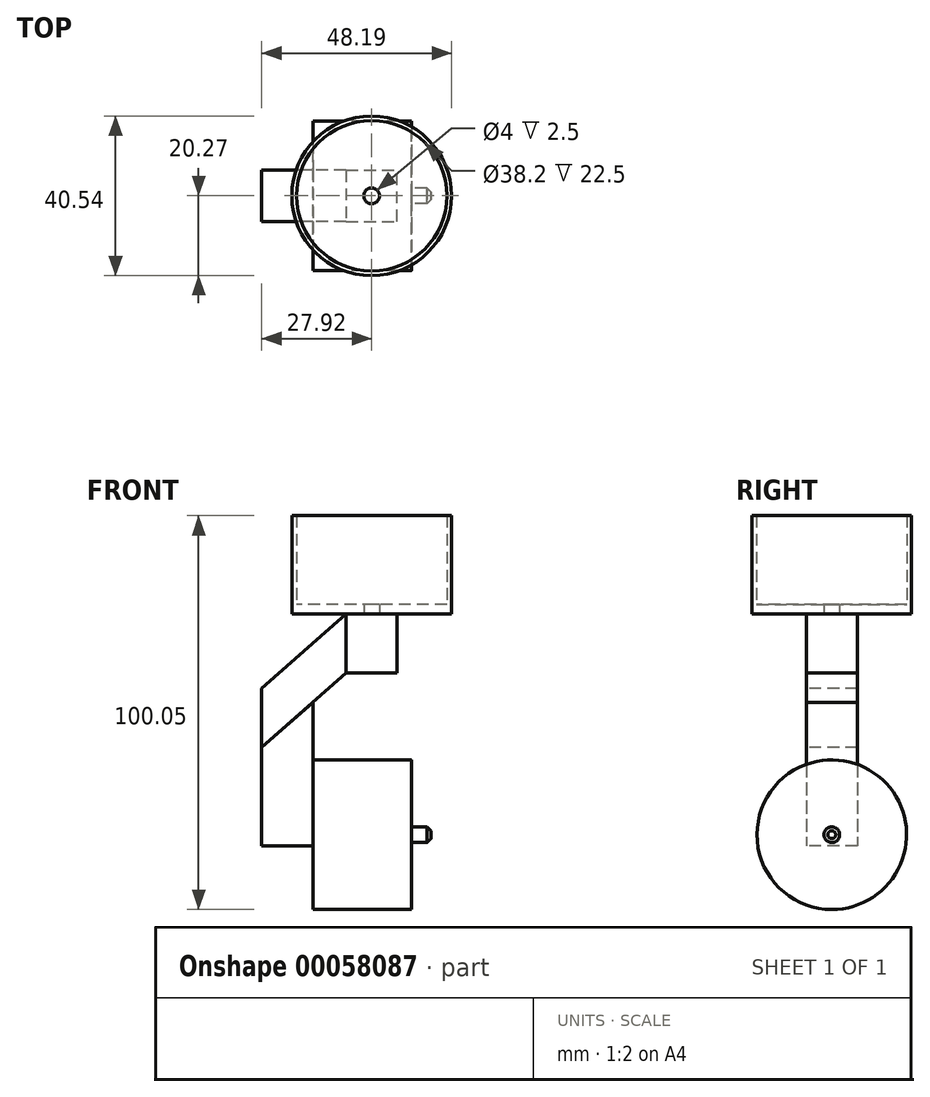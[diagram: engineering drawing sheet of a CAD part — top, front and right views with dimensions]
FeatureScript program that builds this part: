
annotation { "Feature Type Name" : "Feature", "Feature Type Description" : "" }
export const myFeature = defineFeature(function(context is Context, id is Id, definition is map)
    precondition{}
    {
        {
            var Q0;
            Q0=qCreatedBy(makeId("Top.planeOp"),FACE);
            var sketch = newSketch(context, id + "F0", { "sketchPlane" : qUnion([Q0])});
            skCircle(sketch, "E0", {"center": v(0, 0) * mm, "radius": 19.1 * mm});
            skCircle(sketch, "E1", {"center": v(0, 0) * mm, "radius": 20.27 * mm});
            skCircle(sketch, "E2", {"center": v(0, 0) * mm, "radius": 2 * mm});
            skSolve(sketch);
        }
        {
            var Q0;
            Q0=makeQuery(id+"F0.imprint","IMPRINT",FACE,{"disambiguationData":[TD([[makeQuery(id+"F0.imprint","IMPRINT",EDGE,{"derivedFrom":sQuery(id+"F0.wireOp",EDGE,"E0")}),1.0]])]});
            extrude(context, id + "F1", {"entities" : qUnion([Q0]), "depth" : 2.5 * mm});
        }
        {
            var Q0;
            Q0 = qSketchRegion(id + "F0", true);
            extrude(context, id + "F2", {"entities" : qUnion([Q0]), "operationType" : NewBodyOperationType.ADD, "depth" : 25 * mm});
        }
        {
            var Q0;
            {var subQ0=sQuery(id+"F0.wireOp",EDGE,"E0");Q0=makeQuery(id+"F2.boolean.opBoolean","MERGE",FACE,{"derivedFrom":[makeQuery(id+"F1.opExtrude","CAP_FACE",FACE,{"disambiguationData":[OSD([subQ0,sQuery(id+"F0.wireOp",EDGE,"E2")])],"isStart":true}),makeQuery(id+"F2.opExtrude","CAP_FACE",FACE,{"disambiguationData":[OSD([subQ0,sQuery(id+"F0.wireOp",EDGE,"E1")])],"isStart":true})]});}
            var sketch = newSketch(context, id + "F3", { "sketchPlane" : qUnion([Q0])});
            skLineSegment(sketch, "E3.rect.bottom", {"start": v(-6.5, 6.5) * mm, "end": v(6.5, 6.5) * mm});
            skLineSegment(sketch, "E3.rect.top", {"start": v(-6.5, -6.5) * mm, "end": v(6.5, -6.5) * mm});
            skLineSegment(sketch, "E3.rect.left", {"start": v(-6.5, 6.5) * mm, "end": v(-6.5, -6.5) * mm});
            skLineSegment(sketch, "E3.rect.right", {"start": v(6.5, 6.5) * mm, "end": v(6.5, -6.5) * mm});
            skPoint(sketch, "E3.rect.middle", {"position": v(0, 0) * mm});
            skSolve(sketch);
        }
        {
            var Q0;
            Q0=makeQuery(id+"F3.imprint","IMPRINT",FACE,{"disambiguationData":[TD([[makeQuery(id+"F3.imprint","IMPRINT",EDGE,{"derivedFrom":makeQuery(id+"F1.opExtrude","CAP_EDGE",EDGE,{"disambiguationData":[OSD([sQuery(id+"F0.wireOp",EDGE,"E2")])],"isStart":true})}),-1.0]])]});
            var Q1;
            Q1=makeQuery(id+"F3.imprint","IMPRINT",FACE,{"disambiguationData":[TD([[makeQuery(id+"F3.imprint","IMPRINT",EDGE,{"derivedFrom":sQuery(id+"F3.wireOp",EDGE,"E3.rect.bottom")}),-1.0]])]});
            extrude(context, id + "F4", {"entities" : qUnion([Q0, Q1]), "operationType" : NewBodyOperationType.ADD, "depth" : 15 * mm});
        }
        {
            var Q0;
            Q0=makeQuery(id+"F4.opExtrude","SWEPT_FACE",FACE,{"disambiguationData":[OSD([sQuery(id+"F3.wireOp",EDGE,"E3.rect.bottom")])]});
            var sketch = newSketch(context, id + "F5", { "sketchPlane" : qUnion([Q0])});
            skLineSegment(sketch, "E4", {"start": v(-6.5, -15) * mm, "end": v(-27.92, -33.91) * mm});
            skLineSegment(sketch, "E5", {"start": v(-27.92, -33.91) * mm, "end": v(-27.92, -18.91) * mm});
            skLineSegment(sketch, "E6", {"start": v(-6.5, 0) * mm, "end": v(-27.92, -18.91) * mm});
            skSolve(sketch);
        }
        {
            var Q0;
            Q0=makeQuery(id+"F5.imprint","IMPRINT",FACE,{"disambiguationData":[TD([[makeQuery(id+"F5.imprint","IMPRINT",EDGE,{"derivedFrom":sQuery(id+"F5.wireOp",EDGE,"E4")}),-1.0]])]});
            extrude(context, id + "F6", {"entities" : qUnion([Q0]), "oppositeDirection" : true, "depth" : 13 * mm});
        }
        {
            var Q0;
            Q0=makeQuery(id+"F6.opExtrude","CAP_FACE",FACE,{"disambiguationData":[OSD([sQuery(id+"F3.wireOp",EDGE,"E3.rect.bottom"),sQuery(id+"F3.wireOp",EDGE,"E3.rect.left"),sQuery(id+"F5.wireOp",EDGE,"E4"),sQuery(id+"F5.wireOp",EDGE,"E5"),sQuery(id+"F5.wireOp",EDGE,"E6")])],"isStart":true});
            var sketch = newSketch(context, id + "F7", { "sketchPlane" : qUnion([Q0])});
            skLineSegment(sketch, "E7", {"start": v(-27.92, -33.91) * mm, "end": v(-27.92, -58.9) * mm});
            skLineSegment(sketch, "E8", {"start": v(-14.92, -22.43) * mm, "end": v(-14.92, -58.93) * mm});
            skLineSegment(sketch, "E9", {"start": v(-14.92, -58.93) * mm, "end": v(-27.92, -58.9) * mm});
            skSolve(sketch);
        }
        {
            var Q0;
            Q0 = qSketchRegion(id + "F7", true);
            var Q1;
            {var subQ0=sQuery(id+"F7.wireOp",EDGE,"E7");Q1=makeQuery(id+"F7.imprint","IMPRINT",FACE,{"disambiguationData":[TD([[makeQuery(id+"F7.imprint","IMPRINT",EDGE,{"derivedFrom":subQ0}),1.0]])]});}
            extrude(context, id + "F8", {"entities" : qUnion([Q0, Q1]), "oppositeDirection" : true, "depth" : 13 * mm});
        }
        {
            var Q0;
            Q0=makeQuery(id+"F8.opExtrude","SWEPT_FACE",FACE,{"disambiguationData":[OSD([sQuery(id+"F7.wireOp",EDGE,"E8")])]});
            var sketch = newSketch(context, id + "F9", { "sketchPlane" : qUnion([Q0])});
            skCircle(sketch, "E10", {"center": v(0, -56.05) * mm, "radius": 19 * mm});
            skSolve(sketch);
        }
        {
            var Q0;
            {var subQ1=sQuery(id+"F7.wireOp",EDGE,"E8");var subQ6=makeQuery(id+"F8.opExtrude","SWEPT_EDGE",EDGE,{"disambiguationData":[OSD([subQ1,sQuery(id+"F7.wireOp",EDGE,"E9")])]});Q0=makeQuery(id+"F9.imprint","IMPRINT",FACE,{"disambiguationData":[TD([[makeQuery(id+"F9.imprint","IMPRINT",EDGE,{"derivedFrom":subQ6}),-1.0]])]});}
            var Q1;
            {var subQ1=sQuery(id+"F7.wireOp",EDGE,"E8");var subQ6=makeQuery(id+"F8.opExtrude","SWEPT_EDGE",EDGE,{"disambiguationData":[OSD([subQ1,sQuery(id+"F7.wireOp",EDGE,"E9")])]});Q1=makeQuery(id+"F9.imprint","IMPRINT",FACE,{"disambiguationData":[TD([[makeQuery(id+"F9.imprint","IMPRINT",EDGE,{"derivedFrom":subQ6}),1.0]])]});}
            extrude(context, id + "F10", {"entities" : qUnion([Q0, Q1]), "operationType" : NewBodyOperationType.ADD, "depth" : 25 * mm});
        }
        {
            var Q0;
            Q0=makeQuery(id+"F10.opExtrude","CAP_FACE",FACE,{"disambiguationData":[OSD([sQuery(id+"F9.wireOp",EDGE,"E10")])],"isStart":false});
            var sketch = newSketch(context, id + "F11", { "sketchPlane" : qUnion([Q0])});
            skCircle(sketch, "E11", {"center": v(0, -56.05) * mm, "radius": 2 * mm});
            skSolve(sketch);
        }
        {
            var Q0;
            Q0 = qSketchRegion(id + "F11", true);
            var Q1;
            Q1=makeQuery(id+"F11.imprint","IMPRINT",FACE,{"disambiguationData":[TD([[makeQuery(id+"F11.imprint","IMPRINT",EDGE,{"derivedFrom":sQuery(id+"F11.wireOp",EDGE,"E11")}),1.0]])]});
            extrude(context, id + "F12", {"entities" : qUnion([Q0, Q1]), "operationType" : NewBodyOperationType.ADD, "depth" : 5 * mm});
        }
        {
            var Q0;
            Q0=makeQuery(id+"F12.opExtrude","CAP_EDGE",EDGE,{"disambiguationData":[OSD([sQuery(id+"F11.wireOp",EDGE,"E11")])],"isStart":false});
            chamfer(context, id + "F13", {"entities" : qUnion([Q0]), "width" : 1 * mm, "tangentPropagation" : true});
        }
    });
